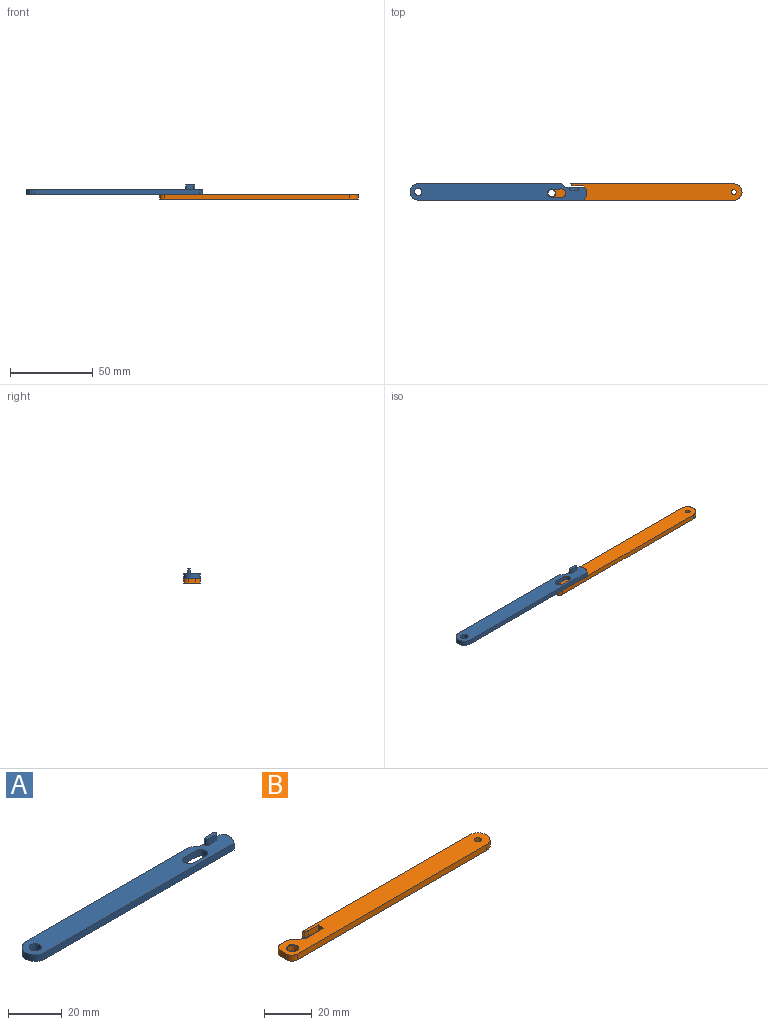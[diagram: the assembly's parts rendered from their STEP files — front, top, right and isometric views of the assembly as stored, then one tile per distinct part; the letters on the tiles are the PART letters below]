
ASSEMBLY  parts=2 mates=1
PART A: 20 faces, bbox 107.1x10x6 mm
  f0: plane 107.1x10mm, normal (0,0,1), area 951.3mm2, adj f1,f2,f3,f4,f5,f6,f7,f8
  f1: cylinder r=2.5mm len=3mm, axis (0,0,-1), area 6.1mm2, adj f0,f7,f11,f12
  f2: cylinder r=2.5mm len=3mm, axis (0,0,-1), area 11.6mm2, adj f0,f9,f11,f12
  f3: plane 100x3mm, normal (0,-1,0), area 300mm2, adj f0,f4,f11,f18
  f4: extruded ~7.81x3mm, area 27.8mm2, adj f0,f3,f5,f11
  f5: plane 10.62x3mm, normal (0,1,0), area 31.9mm2, adj f0,f4,f6,f11
  f6: plane 3x2.66mm, normal (0.64,0.77,0), area 10.3mm2, adj f0,f5,f10,f11
  f7: plane 5.55x3mm, normal (0.01,-1,0), area 16.7mm2, adj f0,f1,f8,f11
  f8: cylinder r=2.5mm len=5mm, axis (0,0,-1), area 25.3mm2, adj f0,f7,f9,f11
  f9: plane 4.93x3mm, normal (0,1,0), area 14.8mm2, adj f0,f2,f8,f11
  f10: plane 86.71x3mm, normal (0,1,0), area 260.1mm2, adj f0,f6,f11,f18
  f11: plane 107.1x10mm, normal (0,0,-1), area 959.1mm2, adj f1,f2,f3,f4,f5,f6,f7,f8
  f12: cylinder r=2.25mm len=3mm, axis (0,0,1), area 9.1mm2, adj f0,f1,f2,f11
  f13: plane 3.92x3mm, normal (0,1,0), area 11.8mm2, adj f0,f14,f16,f17
  f14: cylinder r=0.75mm len=3mm, axis (0,0,-1), area 7.2mm2, adj f0,f13,f15,f17
  f15: plane 4x3mm, normal (0,-1,0), area 12mm2, adj f0,f14,f16,f17
  f16: cylinder r=0.76mm len=3mm, axis (0,0,-1), area 7.3mm2, adj f0,f13,f15,f17
  f17: plane 5.5x1.51mm, normal (0,0,1), area 7.8mm2, adj f13,f14,f15,f16
  f18: cylinder r=5mm len=10mm, axis (0,0,1), area 47.1mm2, adj f0,f3,f10,f11
  f19: cylinder r=2.25mm len=4.5mm, axis (0,0,1), area 42.4mm2, adj f0,f11
PART B: 21 faces, bbox 120x10x3 mm
  f0: plane 112x3mm, normal (0,-1,0), area 336mm2, adj f11,f12,f17,f18
  f1: plane 3x0.02mm, normal (1,0,0), area 0.1mm2, adj f11,f12,f18,f19
  f2: plane 98.85x3mm, normal (0,1,0), area 296.6mm2, adj f3,f11,f12,f19
  f3: plane 3x0.69mm, normal (-0.73,-0.68,0), area 2.8mm2, adj f2,f11,f12,f15
  f4: plane 5.97x3mm, normal (0,-1,0), area 17.9mm2, adj f5,f11,f12,f15
  f5: plane 3.37x3mm, normal (-1,0,0), area 10.1mm2, adj f4,f6,f11,f12
  f6: plane 10.88x3mm, normal (0,1,0), area 32.6mm2, adj f5,f7,f11,f12
  f7: cylinder r=2.5mm len=3mm, axis (0,0,-1), area 7.4mm2, adj f6,f8,f11,f12
  f8: plane 4.15x3.26mm, normal (0.62,0.79,0), area 15.8mm2, adj f7,f9,f11,f12
  f9: plane 4.29x3mm, normal (0,1,0), area 12.9mm2, adj f8,f11,f12,f16
  f10: plane 4x3mm, normal (-1,0,0), area 12mm2, adj f11,f12,f16,f17
  f11: plane 120x10.02mm, normal (0,0,1), area 1106.2mm2, adj f0,f1,f2,f3,f4,f5,f6,f7
  f12: plane 120x10.02mm, normal (0,0,-1), area 1109.9mm2, adj f0,f1,f2,f3,f4,f5,f6,f7
  f13: cylinder r=2.25mm len=4.5mm, axis (0,0,1), area 38.9mm2, adj f12,f14
  f14: cone r=2.25mm half-angle=45deg, axis (0,0,1), area 5.3mm2, adj f11,f13
  f15: cylinder r=2mm len=3mm, axis (0,0,-1), area 5mm2, adj f3,f4,f11,f12
  f16: cylinder r=3mm len=3mm, axis (0,0,1), area 14.1mm2, adj f9,f10,f11,f12
  f17: cylinder r=3mm len=3mm, axis (0,0,-1), area 14.1mm2, adj f0,f10,f11,f12
  f18: cylinder r=5mm len=5mm, axis (0,0,1), area 23.6mm2, adj f0,f1,f11,f12
  f19: cylinder r=5mm len=5mm, axis (0,0,-1), area 23.6mm2, adj f1,f2,f11,f12
  f20: cylinder r=1.5mm len=3mm, axis (0,0,-1), area 28.3mm2, adj f11,f12
PLACE A t=(-0.29,0.11,5.75)mm
PLACE B at identity
MATE revolute A.f1 <-> B.f13  axis (0,0,-1) through (28.83,4.37,5.75)mm
